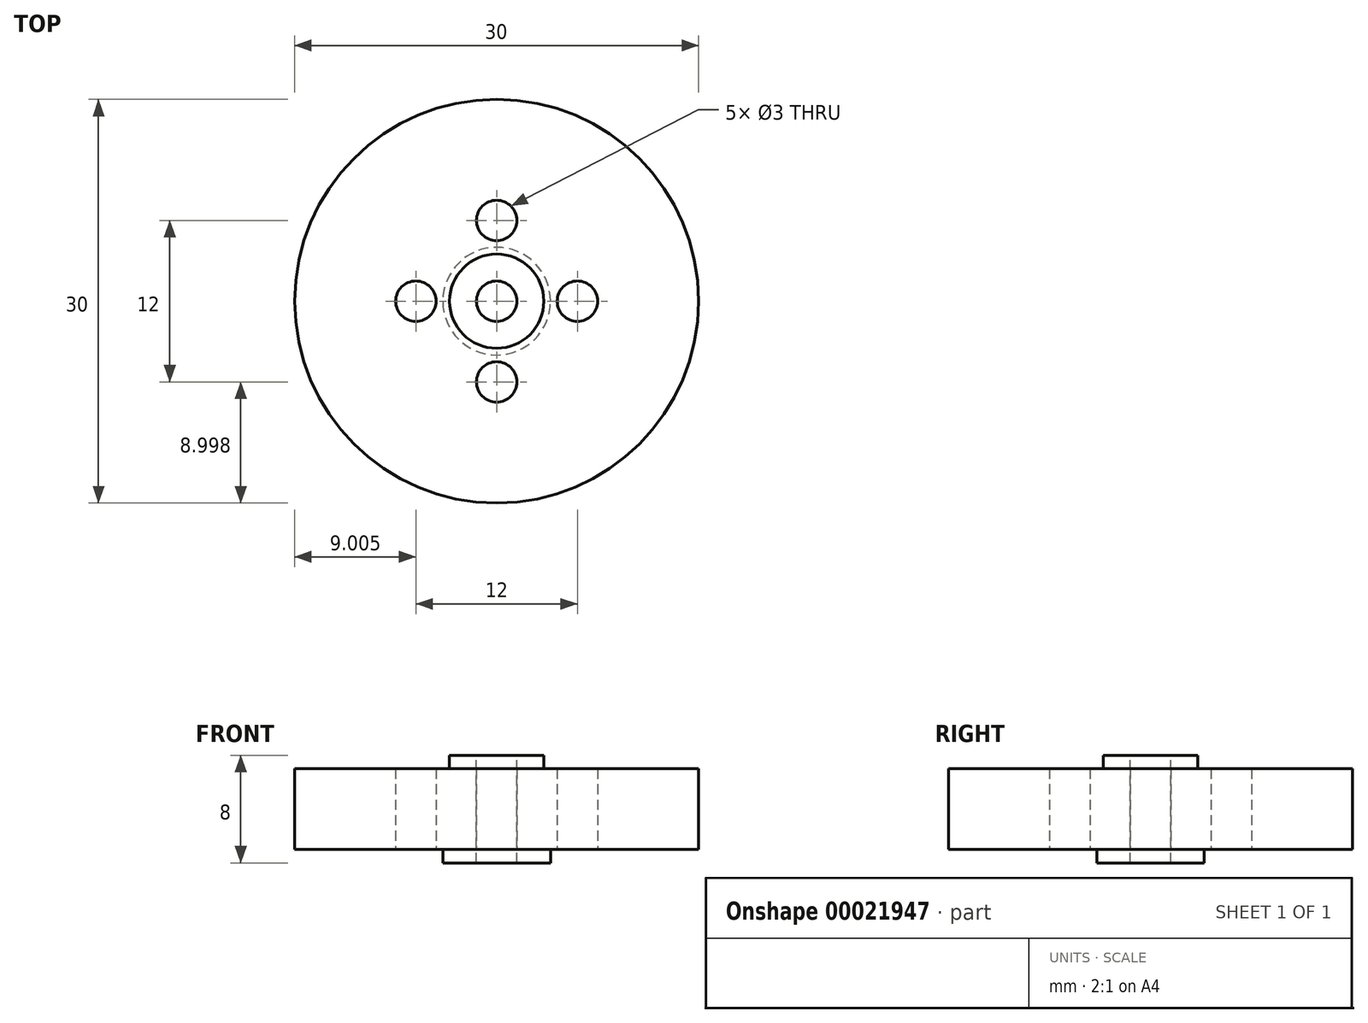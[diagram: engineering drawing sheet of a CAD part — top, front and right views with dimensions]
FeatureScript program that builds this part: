
annotation { "Feature Type Name" : "Feature", "Feature Type Description" : "" }
export const myFeature = defineFeature(function(context is Context, id is Id, definition is map)
    precondition{}
    {
        {
            var Q0;
            Q0=qCreatedBy(makeId("Top.planeOp"),FACE);
            var sketch = newSketch(context, id + "F0", { "sketchPlane" : qUnion([Q0])});
            skCircle(sketch, "E0", {"center": v(-9.55, 3.79) * mm, "radius": 15 * mm});
            skCircle(sketch, "E1", {"center": v(-9.55, 9.79) * mm, "radius": 1.5 * mm});
            skCircle(sketch, "E2.1.0", {"center": v(-15.55, 3.79) * mm, "radius": 1.5 * mm});
            skCircle(sketch, "E2.2.0", {"center": v(-9.55, -2.21) * mm, "radius": 1.5 * mm});
            skCircle(sketch, "E2.3.0", {"center": v(-3.55, 3.79) * mm, "radius": 1.5 * mm});
            skSolve(sketch);
        }
        {
            var Q0;
            Q0=makeQuery(id+"F0.imprint","IMPRINT",FACE,{"disambiguationData":[TD([[makeQuery(id+"F0.imprint","IMPRINT",EDGE,{"derivedFrom":sQuery(id+"F0.wireOp",EDGE,"E0")}),1.0]])]});
            extrude(context, id + "F1", {"entities" : qUnion([Q0]), "depth" : 6 * mm});
        }
        {
            var Q0;
            Q0=makeQuery(id+"F1.opExtrude","CAP_FACE",FACE,{"disambiguationData":[OSD([sQuery(id+"F0.wireOp",EDGE,"E0"),sQuery(id+"F0.wireOp",EDGE,"E1"),sQuery(id+"F0.wireOp",EDGE,"E2.1.0"),sQuery(id+"F0.wireOp",EDGE,"E2.2.0"),sQuery(id+"F0.wireOp",EDGE,"E2.3.0"),sQuery(id+"F0.wireOp",EDGE,"E2.4.0"),sQuery(id+"F0.wireOp",EDGE,"E2.5.0")])],"isStart":false});
            var sketch = newSketch(context, id + "F2", { "sketchPlane" : qUnion([Q0])});
            skCircle(sketch, "E3", {"center": v(-9.55, 3.79) * mm, "radius": 3.5 * mm});
            skSolve(sketch);
        }
        {
            var Q0;
            Q0=qSketchRegion(id+"F2",true);
            var Q1;
            Q1=makeQuery(id+"F2.imprint","IMPRINT",FACE,{"disambiguationData":[TD([[makeQuery(id+"F2.imprint","IMPRINT",EDGE,{"derivedFrom":sQuery(id+"F2.wireOp",EDGE,"E3")}),1.0]])]});
            extrude(context, id + "F3", {"entities" : qUnion([Q0, Q1]), "operationType" : NewBodyOperationType.ADD, "depth" : 1 * mm});
        }
        {
            var Q0;
            Q0=makeQuery(id+"F3.opExtrude","CAP_FACE",FACE,{"disambiguationData":[OSD([sQuery(id+"F2.wireOp",EDGE,"E3")])],"isStart":false});
            var sketch = newSketch(context, id + "F4", { "sketchPlane" : qUnion([Q0])});
            skCircle(sketch, "E4", {"center": v(-9.55, 3.79) * mm, "radius": 1.5 * mm});
            skSolve(sketch);
        }
        {
            var Q0;
            Q0=makeQuery(id+"F4.imprint","IMPRINT",FACE,{"disambiguationData":[TD([[makeQuery(id+"F4.imprint","IMPRINT",EDGE,{"derivedFrom":sQuery(id+"F4.wireOp",EDGE,"E4")}),1.0]])]});
            extrude(context, id + "F5", {"entities" : qUnion([Q0]), "operationType" : NewBodyOperationType.REMOVE, "oppositeDirection" : true, "depth" : 25 * mm});
        }
        {
            var Q0;
            Q0=makeQuery(id+"F1.opExtrude","CAP_FACE",FACE,{"disambiguationData":[OSD([sQuery(id+"F0.wireOp",EDGE,"E0"),sQuery(id+"F0.wireOp",EDGE,"E1"),sQuery(id+"F0.wireOp",EDGE,"E2.1.0"),sQuery(id+"F0.wireOp",EDGE,"E2.2.0"),sQuery(id+"F0.wireOp",EDGE,"E2.3.0"),sQuery(id+"F0.wireOp",EDGE,"E2.4.0"),sQuery(id+"F0.wireOp",EDGE,"E2.5.0")])],"isStart":true});
            var sketch = newSketch(context, id + "F6", { "sketchPlane" : qUnion([Q0])});
            skCircle(sketch, "E5", {"center": v(-9.55, -3.79) * mm, "radius": 4 * mm});
            skSolve(sketch);
        }
        {
            var Q0;
            Q0=makeQuery(id+"F6.imprint","IMPRINT",FACE,{"disambiguationData":[TD([[makeQuery(id+"F6.imprint","IMPRINT",EDGE,{"derivedFrom":sQuery(id+"F6.wireOp",EDGE,"E5")}),1.0]])]});
            extrude(context, id + "F7", {"entities" : qUnion([Q0]), "operationType" : NewBodyOperationType.ADD, "depth" : 1 * mm});
        }
    });
